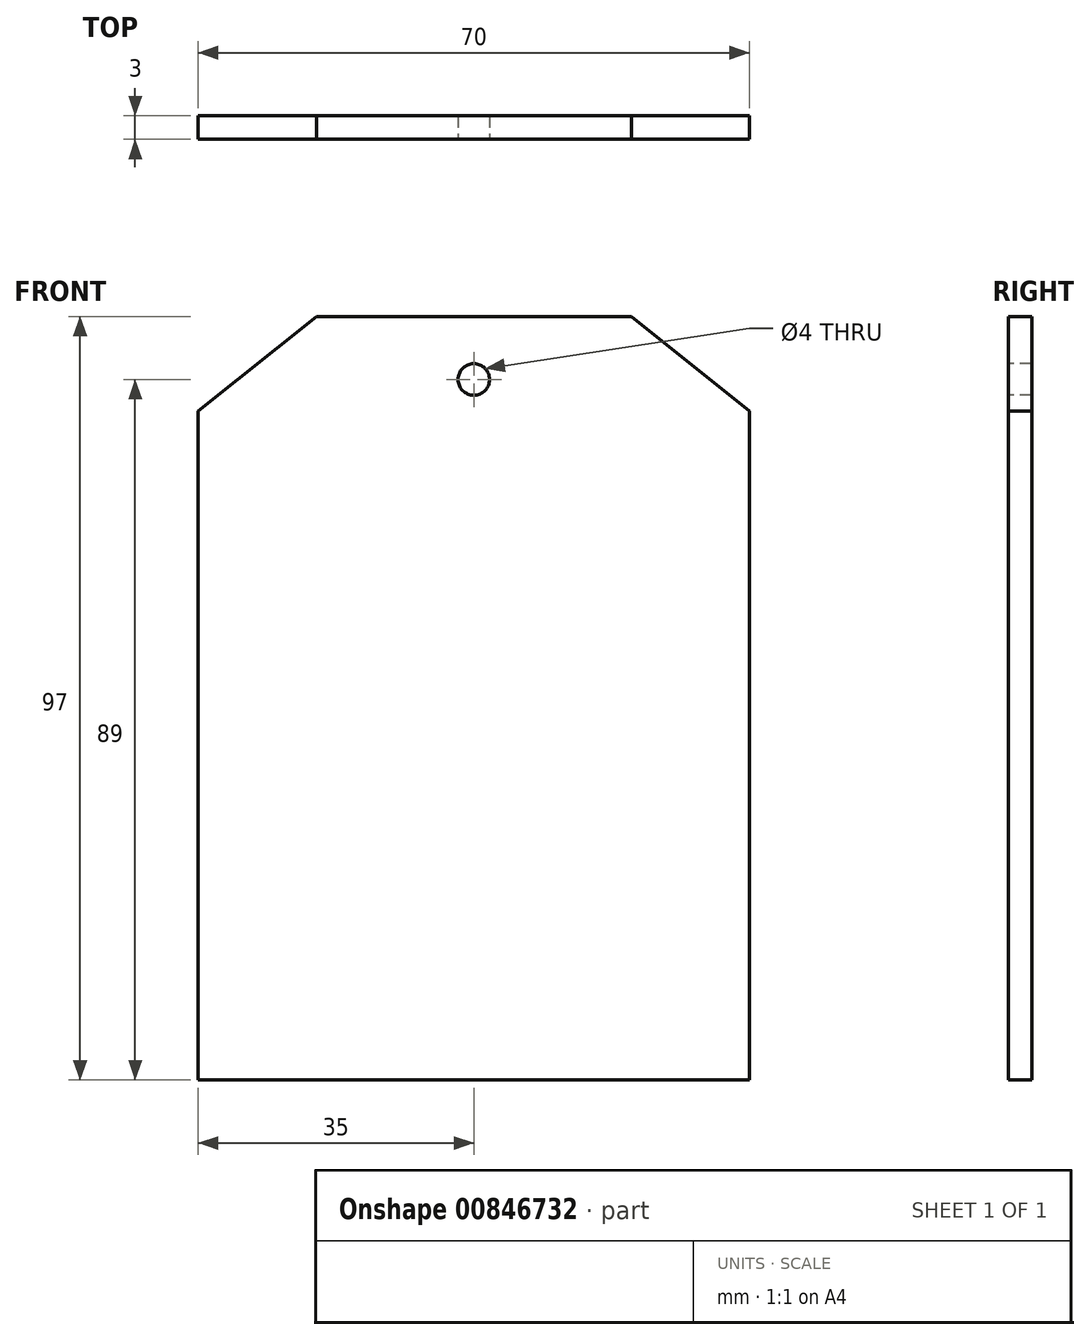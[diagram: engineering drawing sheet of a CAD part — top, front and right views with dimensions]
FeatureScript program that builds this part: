
annotation { "Feature Type Name" : "Feature", "Feature Type Description" : "" }
export const myFeature = defineFeature(function(context is Context, id is Id, definition is map)
    precondition{}
    {
        {
            var Q0;
            Q0=qCreatedBy(makeId("Front.planeOp"),FACE);
            var sketch = newSketch(context, id + "F0", { "sketchPlane" : qUnion([Q0])});
            skLineSegment(sketch, "E0", {"start": v(0, 0) * mm, "end": v(35, 0) * mm});
            skLineSegment(sketch, "E1", {"start": v(35, 0) * mm, "end": v(35, 97) * mm});
            skLineSegment(sketch, "E2", {"start": v(35, 97) * mm, "end": v(0, 97) * mm});
            skLineSegment(sketch, "E3.MirrorCS", {"start": v(-35, 0) * mm, "end": v(-35, 97) * mm});
            skLineSegment(sketch, "E4.MirrorCS", {"start": v(-35, 97) * mm, "end": v(0, 97) * mm});
            skLineSegment(sketch, "E5.MirrorCS", {"start": v(0, 0) * mm, "end": v(-35, 0) * mm});
            skCircle(sketch, "E6", {"center": v(0, 89) * mm, "radius": 2 * mm});
            skSolve(sketch);
        }
        {
            var Q0;
            Q0 = qSketchRegion(id + "F0", true);
            extrude(context, id + "F1", {"entities" : qUnion([Q0]), "oppositeDirection" : true, "depth" : 3 * mm, "offsetDistance" : 25 * mm});
        }
        {
            var Q0;
            Q0=makeQuery(id+"F1.opExtrude","SWEPT_EDGE",EDGE,{"disambiguationData":[OSD([sQuery(id+"F0.wireOp",EDGE,"E3.MirrorCS"),sQuery(id+"F0.wireOp",EDGE,"E4.MirrorCS")])]});
            var Q1;
            Q1=makeQuery(id+"F1.opExtrude","SWEPT_EDGE",EDGE,{"disambiguationData":[OSD([sQuery(id+"F0.wireOp",EDGE,"E1"),sQuery(id+"F0.wireOp",EDGE,"E2")])]});
            chamfer(context, id + "F2", {"entities" : qUnion([Q0, Q1]), "chamferType" : ChamferType.TWO_OFFSETS, "width1" : 15 * mm, "oppositeDirection" : false, "width2" : 12 * mm, "tangentPropagation" : true});
        }
    });
